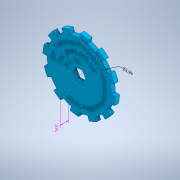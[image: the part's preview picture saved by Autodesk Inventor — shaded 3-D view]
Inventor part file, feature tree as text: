
AUTODESK INVENTOR PART (.ipt)
format: ipt  version: 2021.2 (Build 252289000, 289)  size: 1,675,776 bytes
history: native  units: in
note: dims shown in document units (in); Inventor stores cm internally (conversion verified against a paired STEP export)
features: sketch x5, extrude x4, other x3, pattern_circular x1, revolve x1, split x1
ambient origin geometry x8: Origin, YZ Plane, XZ Plane, XY Plane, X Axis, Y Axis, Z Axis, Center Point
bodies: Solid1 (feature_tree)
feature tree (15):
  other  "Annotations"
  extrude  "Extrusion1"  Depth=0.375in TaperAngle=0.0deg
  extrude  "Extrusion11"  TaperAngle=0.0deg  [1 undecoded]
  extrude  "Extrusion19"  Depth=0.0069in
  pattern_circular  "Circular Pattern11"  [2 undecoded]
  extrude  "Extrusion26"  Depth=0.125in
  revolve  "Revolution2"  Angle=360.0deg
  split  "Split2"
  sketch  "Sketch1"  dims[d0=2.985in d1=0.375in d2=0.0in]
  sketch  "Sketch10"  dims[d55=0.515in d56=0.0in d57=0.0in]
  sketch  "Sketch17"  dims[d123=0.1963in d124=0.0069in]
  sketch  "Sketch28"  dims[d125=0.0893in]
  sketch  "Sketch34"  dims[d126=0.375in d127=0.0in d128=4.7244in d129=360.0deg d131=2.985in d132=3.3777in d181=2.25in d182=0.05in d183=0.0in d203=0.2in d204=0.1in d205=1.0in d206=0.4in d207=0.125in d208=90.0deg d136=0.375in d184=0.237in d185=2.985in]
  other  "Linear Dimension 2"
  other  "Diameter Dimension 1"
note: 3 required parameter values undecoded (feature->parameter linkage not recoverable at this tier; creation-order binding heuristic only, values carry confidence <= 0.55)
